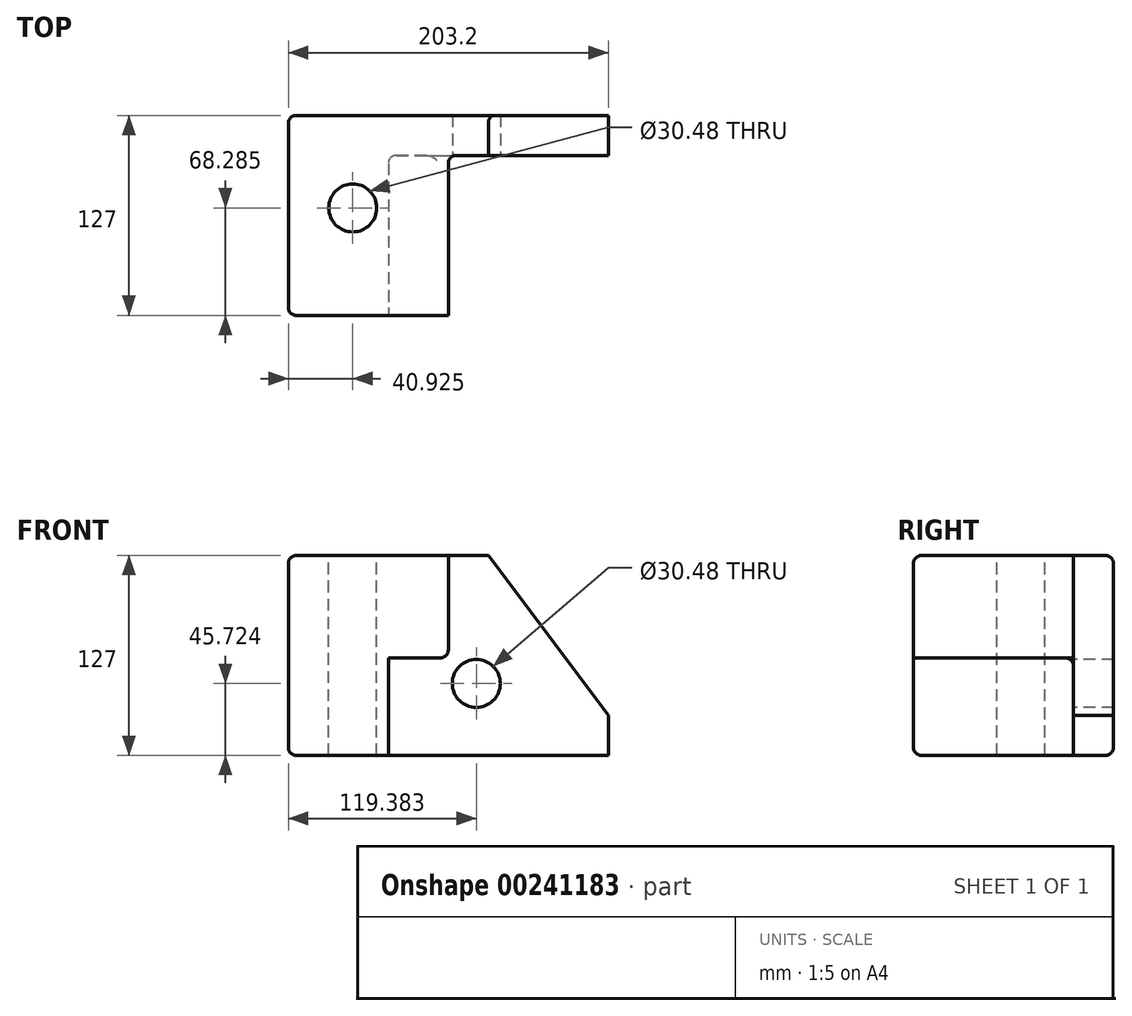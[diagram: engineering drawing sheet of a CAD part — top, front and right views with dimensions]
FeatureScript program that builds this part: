
annotation { "Feature Type Name" : "Feature", "Feature Type Description" : "" }
export const myFeature = defineFeature(function(context is Context, id is Id, definition is map)
    precondition{}
    {
        {
            var Q0;
            Q0=qCreatedBy(makeId("Front.planeOp"),FACE);
            var sketch = newSketch(context, id + "F0", { "sketchPlane" : qUnion([Q0])});
            skLineSegment(sketch, "E0", {"start": v(-80.79, 65.06) * mm, "end": v(-80.79, -61.94) * mm});
            skLineSegment(sketch, "E1", {"start": v(-80.79, -61.94) * mm, "end": v(122.41, -61.94) * mm});
            skLineSegment(sketch, "E2", {"start": v(122.41, -61.94) * mm, "end": v(122.41, 65.06) * mm});
            skLineSegment(sketch, "E3", {"start": v(122.41, 65.06) * mm, "end": v(-80.79, 65.06) * mm});
            skSolve(sketch);
        }
        {
            var Q0;
            Q0=makeQuery(id+"F0.imprint","IMPRINT",FACE,{"disambiguationData":[TD([[makeQuery(id+"F0.imprint","IMPRINT",EDGE,{"derivedFrom":sQuery(id+"F0.wireOp",EDGE,"E0")}),1.0]])]});
            extrude(context, id + "F1", {"entities" : qUnion([Q0]), "depth" : 127 * mm});
        }
        {
            var Q0;
            Q0=makeQuery(id+"F1.opExtrude","CAP_FACE",FACE,{"disambiguationData":[OSD([sQuery(id+"F0.wireOp",EDGE,"E0"),sQuery(id+"F0.wireOp",EDGE,"E1"),sQuery(id+"F0.wireOp",EDGE,"E2"),sQuery(id+"F0.wireOp",EDGE,"E3")])],"isStart":false});
            var sketch = newSketch(context, id + "F2", { "sketchPlane" : qUnion([Q0])});
            skLineSegment(sketch, "E4", {"start": v(-80.79, 65.06) * mm, "end": v(20.81, 65.06) * mm});
            skLineSegment(sketch, "E5", {"start": v(20.81, 65.06) * mm, "end": v(20.81, 0) * mm});
            skLineSegment(sketch, "E6", {"start": v(20.81, 0) * mm, "end": v(-17.29, 0) * mm});
            skLineSegment(sketch, "E7", {"start": v(-17.29, 0) * mm, "end": v(-17.29, -61.94) * mm});
            skLineSegment(sketch, "E8", {"start": v(-17.29, -61.94) * mm, "end": v(-80.79, -61.94) * mm});
            skLineSegment(sketch, "E9", {"start": v(-80.79, -61.94) * mm, "end": v(-80.79, 65.06) * mm});
            skSolve(sketch);
        }
        {
            var Q0;
            {var subQ3=sQuery(id+"F2.wireOp",EDGE,"E5");Q0=makeQuery(id+"F2.imprint","IMPRINT",FACE,{"disambiguationData":[TD([[makeQuery(id+"F2.imprint","IMPRINT",EDGE,{"derivedFrom":subQ3}),1.0]])]});}
            extrude(context, id + "F3", {"entities" : qUnion([Q0]), "operationType" : NewBodyOperationType.REMOVE, "oppositeDirection" : true, "depth" : 101.6 * mm});
        }
        {
            var Q0;
            Q0=makeQuery(id+"F1.opExtrude","SWEPT_EDGE",EDGE,{"disambiguationData":[OSD([sQuery(id+"F0.wireOp",EDGE,"E2"),sQuery(id+"F0.wireOp",EDGE,"E3")])]});
            chamfer(context, id + "F4", {"entities" : qUnion([Q0]), "chamferType" : ChamferType.TWO_OFFSETS, "width1" : 76.2 * mm, "oppositeDirection" : false, "width2" : 101.6 * mm, "tangentPropagation" : true});
        }
        {
            var Q0;
            Q0=makeQuery(id+"F1.opExtrude","CAP_EDGE",EDGE,{"disambiguationData":[OSD([sQuery(id+"F0.wireOp",EDGE,"E3")])],"isStart":false});
            var Q1;
            Q1=makeQuery(id+"F3.boolean.opBoolean","COPY",EDGE,{"derivedFrom":makeQuery(id+"F3.opExtrude","SWEPT_EDGE",EDGE,{"disambiguationData":[OSD([sQuery(id+"F0.wireOp",EDGE,"E3"),sQuery(id+"F2.wireOp",EDGE,"E4"),sQuery(id+"F2.wireOp",EDGE,"E5")])]})});
            var Q2;
            Q2=makeQuery(id+"F3.boolean.opBoolean","COPY",EDGE,{"derivedFrom":makeQuery(id+"F3.opExtrude","CAP_EDGE",EDGE,{"disambiguationData":[OSD([sQuery(id+"F2.wireOp",EDGE,"E5")])],"isStart":false})});
            var Q3;
            Q3=makeQuery(id+"F3.boolean.opBoolean","COPY",EDGE,{"derivedFrom":makeQuery(id+"F3.opExtrude","SWEPT_EDGE",EDGE,{"disambiguationData":[OSD([sQuery(id+"F2.wireOp",EDGE,"E5"),sQuery(id+"F2.wireOp",EDGE,"E6")])]})});
            var Q4;
            Q4=makeQuery(id+"F3.boolean.opBoolean","COPY",EDGE,{"derivedFrom":makeQuery(id+"F3.opExtrude","CAP_EDGE",EDGE,{"disambiguationData":[OSD([sQuery(id+"F2.wireOp",EDGE,"E6")])],"isStart":true})});
            var Q5;
            Q5=makeQuery(id+"F3.boolean.opBoolean","COPY",EDGE,{"derivedFrom":makeQuery(id+"F3.opExtrude","CAP_EDGE",EDGE,{"disambiguationData":[OSD([sQuery(id+"F2.wireOp",EDGE,"E5")])],"isStart":true})});
            var Q6;
            Q6=makeQuery(id+"F3.boolean.opBoolean","COPY",EDGE,{"derivedFrom":makeQuery(id+"F3.opExtrude","CAP_EDGE",EDGE,{"disambiguationData":[OSD([sQuery(id+"F2.wireOp",EDGE,"E7")])],"isStart":true})});
            var Q7;
            Q7=makeQuery(id+"F1.opExtrude","CAP_EDGE",EDGE,{"disambiguationData":[OSD([sQuery(id+"F0.wireOp",EDGE,"E1")])],"isStart":false});
            var Q8;
            Q8=makeQuery(id+"F3.boolean.opBoolean","COPY",EDGE,{"derivedFrom":makeQuery(id+"F3.opExtrude","SWEPT_EDGE",EDGE,{"disambiguationData":[OSD([sQuery(id+"F0.wireOp",EDGE,"E1"),sQuery(id+"F2.wireOp",EDGE,"E7"),sQuery(id+"F2.wireOp",EDGE,"E8")])]})});
            var Q9;
            Q9=makeQuery(id+"F3.boolean.opBoolean","COPY",EDGE,{"derivedFrom":makeQuery(id+"F3.opExtrude","CAP_EDGE",EDGE,{"disambiguationData":[OSD([sQuery(id+"F2.wireOp",EDGE,"E7")])],"isStart":false})});
            var Q10;
            Q10=makeQuery(id+"F1.opExtrude","CAP_EDGE",EDGE,{"disambiguationData":[OSD([sQuery(id+"F0.wireOp",EDGE,"E3")])],"isStart":true});
            var Q11;
            Q11=makeQuery(id+"F1.opExtrude","SWEPT_EDGE",EDGE,{"disambiguationData":[OSD([sQuery(id+"F0.wireOp",EDGE,"E0"),sQuery(id+"F0.wireOp",EDGE,"E3")])]});
            var Q12;
            Q12=makeQuery(id+"F1.opExtrude","CAP_EDGE",EDGE,{"disambiguationData":[OSD([sQuery(id+"F0.wireOp",EDGE,"E0")])],"isStart":false});
            var Q13;
            Q13=makeQuery(id+"F1.opExtrude","SWEPT_EDGE",EDGE,{"disambiguationData":[OSD([sQuery(id+"F0.wireOp",EDGE,"E0"),sQuery(id+"F0.wireOp",EDGE,"E1")])]});
            var Q14;
            Q14=makeQuery(id+"F1.opExtrude","CAP_EDGE",EDGE,{"disambiguationData":[OSD([sQuery(id+"F0.wireOp",EDGE,"E1")])],"isStart":true});
            var Q15;
            Q15=makeQuery(id+"F1.opExtrude","CAP_EDGE",EDGE,{"disambiguationData":[OSD([sQuery(id+"F0.wireOp",EDGE,"E0")])],"isStart":true});
            fillet(context, id + "F5", {"entities" : qUnion([Q0, Q1, Q2, Q3, Q4, Q5, Q6, Q7, Q8, Q9, Q10, Q11, Q12, Q13, Q14, Q15]), "radius" : 5.08 * mm, "tangentPropagation" : true, "allowEdgeOverflow" : false});
        }
        {
            var Q0;
            Q0=makeQuery(id+"F3.boolean.opBoolean","COPY",FACE,{"derivedFrom":makeQuery(id+"F3.opExtrude","CAP_FACE",FACE,{"disambiguationData":[OSD([sQuery(id+"F0.wireOp",EDGE,"E1"),sQuery(id+"F0.wireOp",EDGE,"E2"),sQuery(id+"F0.wireOp",EDGE,"E3"),sQuery(id+"F2.wireOp",EDGE,"E5"),sQuery(id+"F2.wireOp",EDGE,"E6"),sQuery(id+"F2.wireOp",EDGE,"E7")])],"isStart":false})});
            var sketch = newSketch(context, id + "F6", { "sketchPlane" : qUnion([Q0])});
            skCircle(sketch, "E10", {"center": v(38.6, -16.22) * mm, "radius": 15.24 * mm});
            skSolve(sketch);
        }
        {
            var Q0;
            Q0=makeQuery(id+"F6.imprint","IMPRINT",FACE,{"disambiguationData":[TD([[makeQuery(id+"F6.imprint","IMPRINT",EDGE,{"derivedFrom":sQuery(id+"F6.wireOp",EDGE,"E10")}),1.0]])]});
            var Q1;
            Q1=sQuery(id+"F6.wireOp",EDGE,"E10");
            extrude(context, id + "F7", {"entities" : qUnion([Q0]), "operationType" : NewBodyOperationType.REMOVE, "surfaceEntities" : qUnion([Q1]), "oppositeDirection" : true, "depth" : 1270 * mm});
        }
        {
            var Q0;
            Q0=makeQuery(id+"F1.opExtrude","SWEPT_FACE",FACE,{"disambiguationData":[OSD([sQuery(id+"F0.wireOp",EDGE,"E3")])]});
            var sketch = newSketch(context, id + "F8", { "sketchPlane" : qUnion([Q0])});
            skCircle(sketch, "E11", {"center": v(-39.87, -58.71) * mm, "radius": 15.24 * mm});
            skSolve(sketch);
        }
        {
            var Q0;
            Q0=makeQuery(id+"F8.imprint","IMPRINT",FACE,{"disambiguationData":[TD([[makeQuery(id+"F8.imprint","IMPRINT",EDGE,{"derivedFrom":sQuery(id+"F8.wireOp",EDGE,"E11")}),1.0]])]});
            var Q1;
            Q1=sQuery(id+"F8.wireOp",EDGE,"E11");
            extrude(context, id + "F9", {"entities" : qUnion([Q0]), "operationType" : NewBodyOperationType.REMOVE, "surfaceEntities" : qUnion([Q1]), "oppositeDirection" : true, "depth" : 12903.2 * mm});
        }
    });
